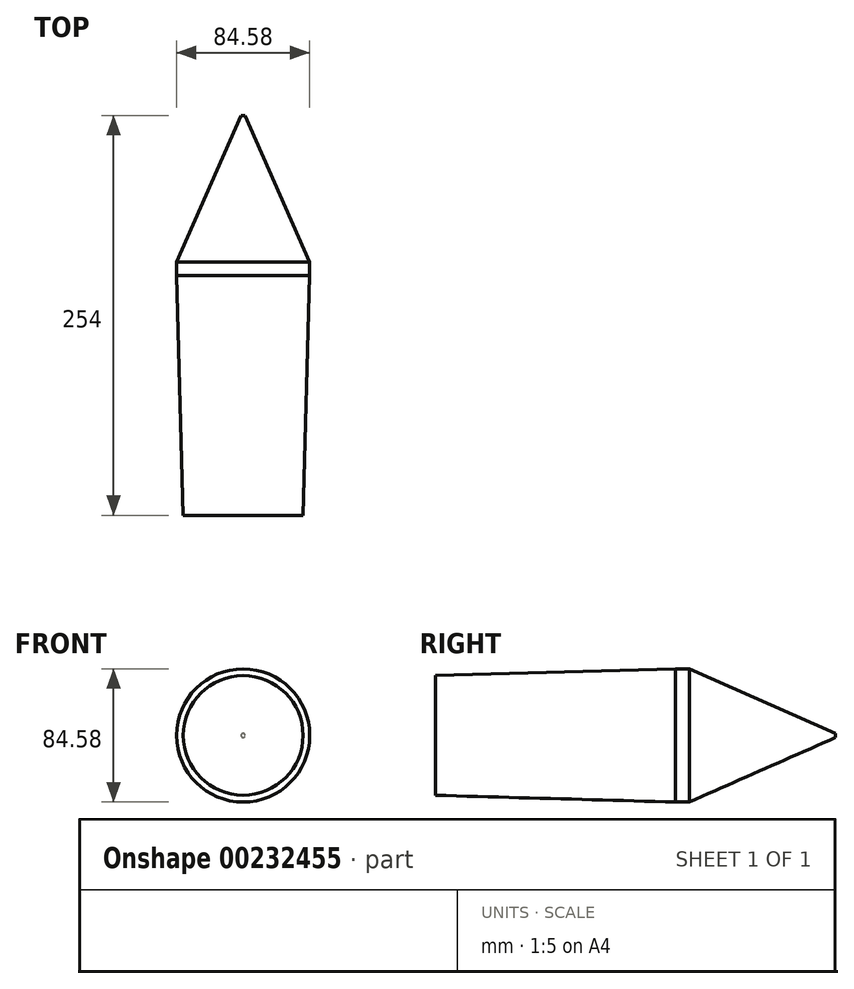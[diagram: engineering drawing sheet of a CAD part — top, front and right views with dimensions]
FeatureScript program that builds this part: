
annotation { "Feature Type Name" : "Feature", "Feature Type Description" : "" }
export const myFeature = defineFeature(function(context is Context, id is Id, definition is map)
    precondition{}
    {
        {
            var Q0;
            Q0=qCreatedBy(makeId("Front.planeOp"),FACE);
            cPlane(context, id + "F0", {"entities" : qUnion([Q0]), "cplaneType" : CPlaneType.OFFSET, "offset" : 152.4 * mm, "width" : 152.4 * mm, "height" : 152.4 * mm});
        }
        {
            var Q0;
            Q0=qCreatedBy(makeId("Front.planeOp"),FACE);
            var sketch = newSketch(context, id + "F1", { "sketchPlane" : qUnion([Q0])});
            skCircle(sketch, "E0", {"center": v(0, 0) * mm, "radius": 42.3 * mm});
            skSolve(sketch);
        }
        {
            var Q0;
            Q0=qCreatedBy(id+"F0.planeOp",FACE);
            var sketch = newSketch(context, id + "F2", { "sketchPlane" : qUnion([Q0])});
            skCircle(sketch, "E1", {"center": v(0, 0) * mm, "radius": 38.04 * mm});
            skSolve(sketch);
        }
        {
            var Q0;
            Q0=makeQuery(id+"F1.imprint","IMPRINT",FACE,{"disambiguationData":[TD([[makeQuery(id+"F1.imprint","IMPRINT",EDGE,{"derivedFrom":sQuery(id+"F1.wireOp",EDGE,"E0")}),1.0]])]});
            var Q1;
            Q1=makeQuery(id+"F2.imprint","IMPRINT",FACE,{"disambiguationData":[TD([[makeQuery(id+"F2.imprint","IMPRINT",EDGE,{"derivedFrom":sQuery(id+"F2.wireOp",EDGE,"E1")}),1.0]])]});
            loft(context, id + "F3", {"sheetProfilesArray" : [{ "sheetProfileEntities" : qUnion([Q0]) }, { "sheetProfileEntities" : qUnion([Q1]) }]});
        }
        {
            var Q0;
            Q0=makeQuery(id+"F3.opLoft","CAP_FACE",FACE,{"disambiguationData":[OSD([makeQuery(id+"F1.imprint","IMPRINT",FACE,{"disambiguationData":[TD([[makeQuery(id+"F1.imprint","IMPRINT",EDGE,{"derivedFrom":sQuery(id+"F1.wireOp",EDGE,"E0")}),1.0]])]})])],"isStart":true});
            extrude(context, id + "F4", {"entities" : qUnion([Q0]), "operationType" : NewBodyOperationType.ADD, "depth" : 8.64 * mm});
        }
        {
            var Q0;
            Q0=qCreatedBy(makeId("Front.planeOp"),FACE);
            cPlane(context, id + "F5", {"entities" : qUnion([Q0]), "cplaneType" : CPlaneType.OFFSET, "offset" : 101.6 * mm, "oppositeDirection" : true, "width" : 152.4 * mm, "height" : 152.4 * mm});
        }
        {
            var Q0;
            Q0=qCreatedBy(id+"F5.planeOp",FACE);
            var sketch = newSketch(context, id + "F6", { "sketchPlane" : qUnion([Q0])});
            skCircle(sketch, "E2", {"center": v(0, 0) * mm, "radius": 1.27 * mm});
            skSolve(sketch);
        }
        {
            var Q1;
            Q1=makeQuery(id+"F4.opExtrude","CAP_FACE",FACE,{"disambiguationData":[OSD([makeQuery(id+"F1.imprint","IMPRINT",FACE,{"disambiguationData":[TD([[makeQuery(id+"F1.imprint","IMPRINT",EDGE,{"derivedFrom":sQuery(id+"F1.wireOp",EDGE,"E0")}),1.0]])]})])],"isStart":false});
            var Q2;
            Q2=makeQuery(id+"F6.imprint","IMPRINT",FACE,{"disambiguationData":[TD([[makeQuery(id+"F6.imprint","IMPRINT",EDGE,{"derivedFrom":sQuery(id+"F6.wireOp",EDGE,"E2")}),1.0]])]});
            loft(context, id + "F7", {"operationType" : NewBodyOperationType.ADD, "sheetProfilesArray" : [{ "sheetProfileEntities" : qUnion([Q1]) }, { "sheetProfileEntities" : qUnion([Q2]) }]});
        }
    });
